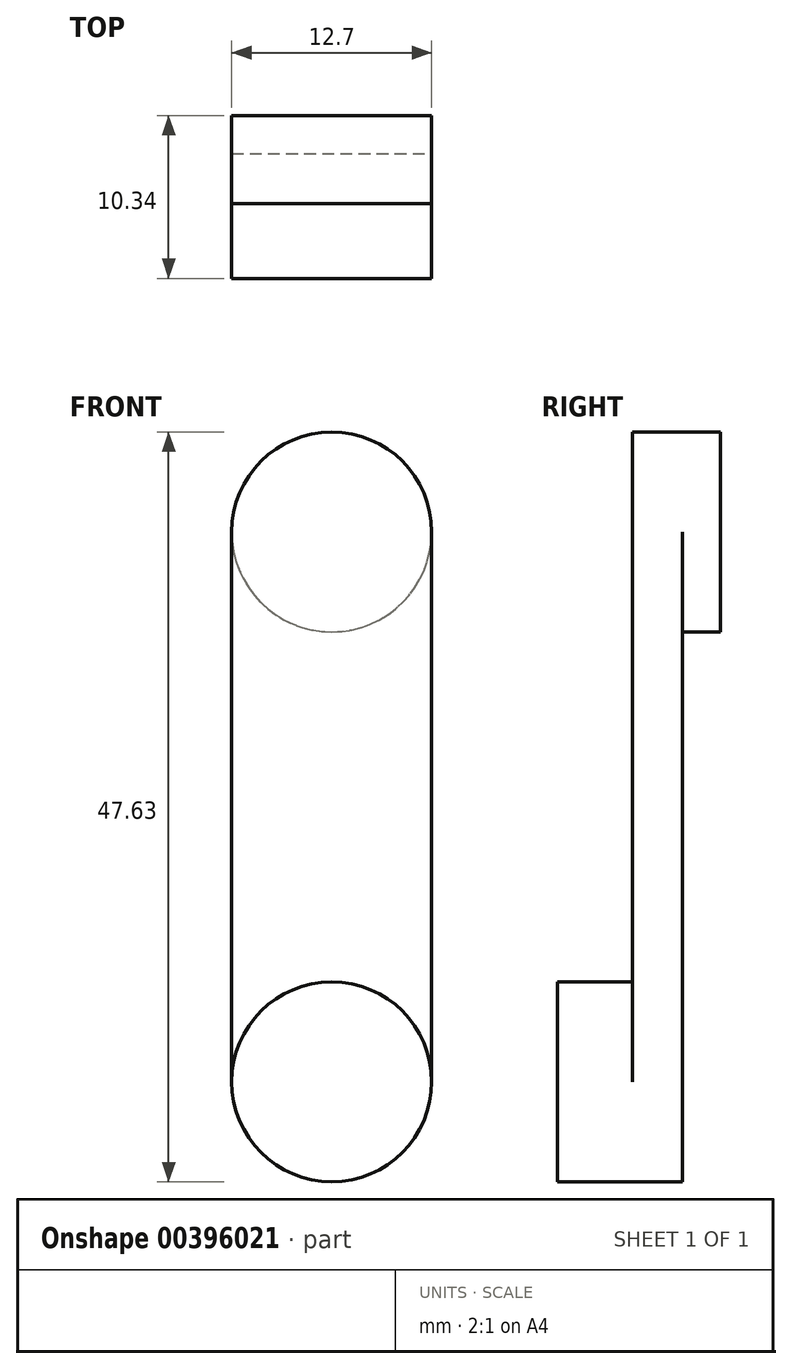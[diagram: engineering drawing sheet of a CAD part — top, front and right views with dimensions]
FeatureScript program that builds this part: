
annotation { "Feature Type Name" : "Feature", "Feature Type Description" : "" }
export const myFeature = defineFeature(function(context is Context, id is Id, definition is map)
    precondition{}
    {
        {
            var Q0;
            Q0=qCreatedBy(makeId("Front.planeOp"),FACE);
            var sketch = newSketch(context, id + "F0", { "sketchPlane" : qUnion([Q0])});
            skCircle(sketch, "E0", {"center": v(0, 0) * mm, "radius": 34.92 * mm, "construction": true});
            skCircle(sketch, "E1", {"center": v(0, 0) * mm, "radius": 19.05 * mm, "construction": true});
            skCircle(sketch, "E2", {"center": v(-5.56, 18.22) * mm, "radius": 3.18 * mm, "construction": true});
            skArc(sketch, "E3", {"start": v(-6.35, -34.92) * mm, "mid": v(0, -41.27) * mm, "end": v(6.35, -34.92) * mm});
            skArc(sketch, "E4", {"start": v(6.35, 0) * mm, "mid": v(0, 6.35) * mm, "end": v(-6.35, 0) * mm});
            skLineSegment(sketch, "E5", {"start": v(-6.35, 0) * mm, "end": v(-6.35, -34.92) * mm});
            skLineSegment(sketch, "E6", {"start": v(6.35, 0) * mm, "end": v(6.35, -34.92) * mm});
            skPoint(sketch, "E7.newPointB", {"position": v(6.35, 0) * mm});
            skSolve(sketch);
        }
        {
            var Q0;
            Q0 = qSketchRegion(id + "F0", true);
            extrude(context, id + "F1", {"entities" : qUnion([Q0]), "depth" : 3.17 * mm, "offsetDistance" : 25.4 * mm});
        }
        {
            var Q0;
            Q0=makeQuery(id+"F1.opExtrude","CAP_FACE",FACE,{"disambiguationData":[OSD([sQuery(id+"F0.wireOp",EDGE,"0fb8d851-721d-4e6b-bb2a-74da2da3602f"),sQuery(id+"F0.wireOp",EDGE,"E3"),sQuery(id+"F0.wireOp",EDGE,"E4"),sQuery(id+"F0.wireOp",EDGE,"E5"),sQuery(id+"F0.wireOp",EDGE,"E6"),sQuery(id+"F0.wireOp",EDGE,"E7.filletArc"),sQuery(id+"F0.wireOp",EDGE,"hccuzMSH-BA4B-Z2h7-681s-I8m0OBSoMAHv"),sQuery(id+"F0.wireOp",EDGE,"f3e137dd-075a-475f-a0b2-5d20c6d22c17.filletArc")])],"isStart":true});
            var sketch = newSketch(context, id + "F2", { "sketchPlane" : qUnion([Q0])});
            skCircle(sketch, "E8", {"center": v(0, 0) * mm, "radius": 6.35 * mm});
            skSolve(sketch);
        }
        {
            var Q0;
            Q0 = qSketchRegion(id + "F2", true);
            extrude(context, id + "F3", {"entities" : qUnion([Q0]), "operationType" : NewBodyOperationType.ADD, "depth" : 2.4 * mm, "offsetDistance" : 25.4 * mm});
        }
        {
            var Q0;
            Q0=makeQuery(id+"F1.opExtrude","CAP_FACE",FACE,{"disambiguationData":[OSD([sQuery(id+"F0.wireOp",EDGE,"E3"),sQuery(id+"F0.wireOp",EDGE,"E4"),sQuery(id+"F0.wireOp",EDGE,"E5"),sQuery(id+"F0.wireOp",EDGE,"E6")])],"isStart":false});
            var sketch = newSketch(context, id + "F4", { "sketchPlane" : qUnion([Q0])});
            skCircle(sketch, "E9", {"center": v(0, -34.92) * mm, "radius": 6.35 * mm});
            skSolve(sketch);
        }
        {
            var Q0;
            Q0 = qSketchRegion(id + "F4", true);
            extrude(context, id + "F5", {"entities" : qUnion([Q0]), "operationType" : NewBodyOperationType.ADD, "depth" : 4.76 * mm, "offsetDistance" : 25.4 * mm});
        }
    });
